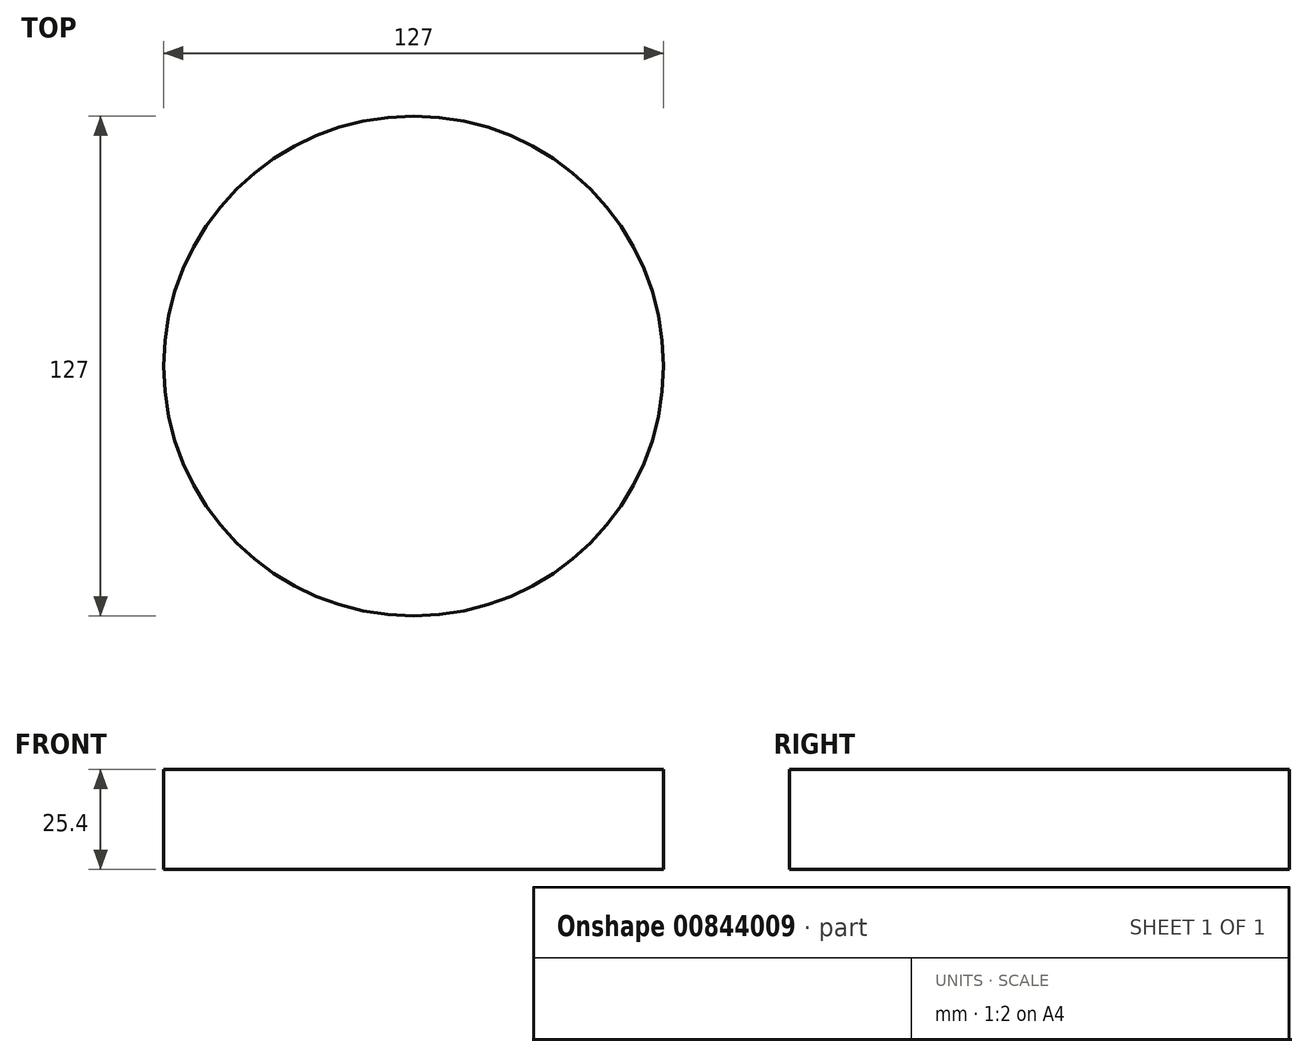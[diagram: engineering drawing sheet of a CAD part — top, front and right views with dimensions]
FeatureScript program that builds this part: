
annotation { "Feature Type Name" : "Feature", "Feature Type Description" : "" }
export const myFeature = defineFeature(function(context is Context, id is Id, definition is map)
    precondition{}
    {
        {
            var Q0;
            Q0=qCreatedBy(makeId("Top.planeOp"),FACE);
            var sketch = newSketch(context, id + "F0", { "sketchPlane" : qUnion([Q0])});
            skCircle(sketch, "E0", {"center": v(0, 0) * mm, "radius": 63.5 * mm});
            skSolve(sketch);
        }
        {
            var Q0;
            Q0=makeQuery(id+"F0.imprint","IMPRINT",FACE,{"disambiguationData":[TD([[makeQuery(id+"F0.imprint","IMPRINT",EDGE,{"derivedFrom":sQuery(id+"F0.wireOp",EDGE,"E0")}),1.0]])]});
            extrude(context, id + "F1", {"entities" : qUnion([Q0]), "depth" : 25.4 * mm, "offsetDistance" : 25.4 * mm});
        }
    });
